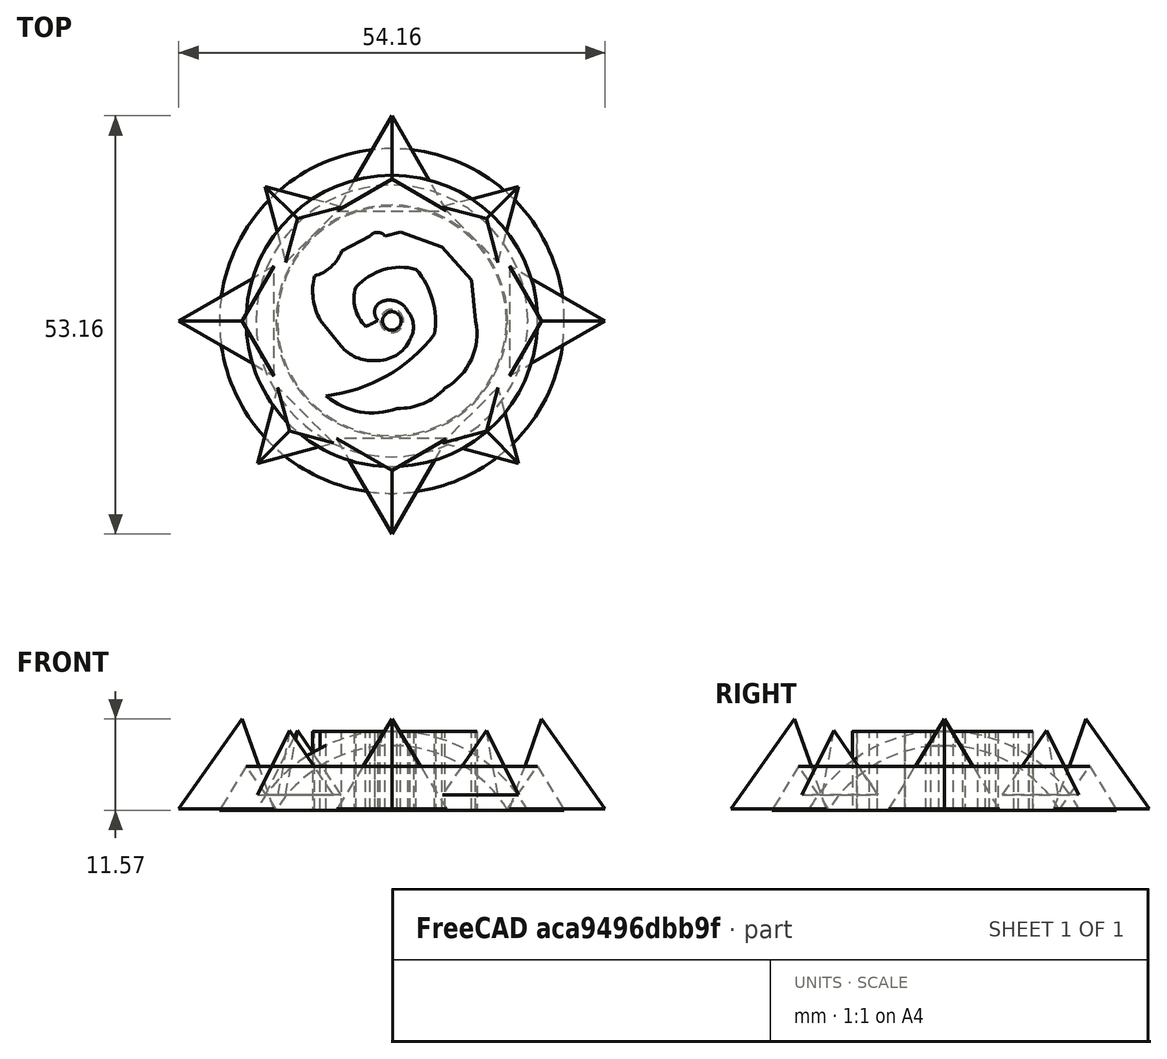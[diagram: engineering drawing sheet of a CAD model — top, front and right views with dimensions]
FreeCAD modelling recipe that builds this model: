
FCSTD DOCUMENT  (FreeCAD 0.19R24291 (Git))
Label: h_brooch_assembly
License: All rights reserved
LicenseURL: http://en.wikipedia.org/wiki/All_rights_reserved
objects: Part::FeaturePython×8, App::DocumentObjectGroup×4, Sketcher::SketchObject×3, PartDesign::Revolution×2, PartDesign::Body×2, Image::ImagePlane×1, Part::Extrusion×1
note: 18 computed .brp shape members not serialized (recipe doc carries the construction recipe); baked Part::Feature solids carry a one-line shape summary decoded from their .brp

FEATURE [Sketcher::SketchObject] Sketch  label="GlowSpiral"
  FullyConstrained = false
  sketch-geometry (22):
    g0: ArcOfCircle CenterX=-0.753903 CenterY=1.11645 CenterZ=0 NormalX=0 NormalY=0 NormalZ=1 AngleXU=0 Radius=1.44543 StartAngle=2.09761 EndAngle=3.93638
    g1: ArcOfCircle CenterX=-0.299965 CenterY=0.00240098 CenterZ=0 NormalX=0 NormalY=0 NormalZ=1 AngleXU=0 Radius=2.64199 StartAngle=0.448711 EndAngle=2.03408
    g2: ArcOfCircle CenterX=-2.56014 CenterY=0.00864041 CenterZ=0 NormalX=0 NormalY=0 NormalZ=1 AngleXU=0 Radius=5.02948 StartAngle=3.82299 EndAngle=4.79664
    g3: ArcOfCircle CenterX=-1.82019 CenterY=-0.475985 CenterZ=0 NormalX=0 NormalY=0 NormalZ=1 AngleXU=0 Radius=4.53808 StartAngle=4.64254 EndAngle=5.86431
    g4: ArcOfCircle CenterX=-0.390387 CenterY=-0.769781 CenterZ=0 NormalX=0 NormalY=0 NormalZ=1 AngleXU=0 Radius=3.12811 StartAngle=5.76403 EndAngle=6.94335
    g5: ArcOfCircle CenterX=1.11392 CenterY=-0.803597 CenterZ=0 NormalX=0 NormalY=0 NormalZ=1 AngleXU=0 Radius=7.62554 StartAngle=1.30785 EndAngle=2.40867
    g6: ArcOfCircle CenterX=-0.0423114 CenterY=2.77393 CenterZ=0 NormalX=0 NormalY=0 NormalZ=1 AngleXU=0 Radius=4.7618 StartAngle=2.81575 EndAngle=3.95354
    g7: ArcOfCircle CenterX=-6.1911 CenterY=7.09486 CenterZ=0 NormalX=0 NormalY=0 NormalZ=1 AngleXU=0 Radius=8.2897 StartAngle=5.06621 EndAngle=5.27544
    g8: ArcOfCircle CenterX=-4.86106 CenterY=-0.147308 CenterZ=0 NormalX=0 NormalY=0 NormalZ=1 AngleXU=0 Radius=10.4068 StartAngle=6.13482 EndAngle=6.98355
    g9: ArcOfCircle CenterX=-10.7491 CenterY=10.7802 CenterZ=0 NormalX=0 NormalY=0 NormalZ=1 AngleXU=0 Radius=20.4256 StartAngle=4.83085 EndAngle=5.62674
    g10: ArcOfCircle CenterX=-2.09735 CenterY=3.86717 CenterZ=0 NormalX=0 NormalY=0 NormalZ=1 AngleXU=0 Radius=7.95781 StartAngle=2.9056 EndAngle=3.63616
    g11: LineSegment StartX=-9.10161 StartY=0.0899867 StartZ=0 EndX=-6.46651 EndY=-3.15932 EndZ=0
    g12: ArcOfCircle CenterX=-11.1957 CenterY=10.7355 CenterZ=0 NormalX=0 NormalY=0 NormalZ=1 AngleXU=0 Radius=5.18935 StartAngle=4.97778 EndAngle=5.91229
    g13: ArcOfCircle CenterX=-1.82628 CenterY=10.0578 CenterZ=0 NormalX=0 NormalY=0 NormalZ=1 AngleXU=0 Radius=1.20224 StartAngle=0.664774 EndAngle=2.5128
    g14: ArcOfCircle CenterX=-2.48457 CenterY=-2.69888 CenterZ=0 NormalX=0 NormalY=0 NormalZ=1 AngleXU=0 Radius=8.97302 StartAngle=4.00215 EndAngle=5.07128
    g15: ArcOfCircle CenterX=0.905868 CenterY=-3.16877 CenterZ=0 NormalX=0 NormalY=0 NormalZ=1 AngleXU=0 Radius=7.93503 StartAngle=4.68229 EndAngle=5.5445
    g16: ArcOfCircle CenterX=2.8748 CenterY=-1.60069 CenterZ=0 NormalX=0 NormalY=0 NormalZ=1 AngleXU=0 Radius=7.93432 StartAngle=5.22593 EndAngle=6.48632
    g17: LineSegment StartX=-6.35919 StartY=8.8546 StartZ=0 EndX=-2.79858 EndY=10.7649 EndZ=0
    g18: LineSegment StartX=1.07314 StartY=11.268 StartZ=0 EndX=6.34907 EndY=9.42071 EndZ=0
    g19: LineSegment StartX=6.34907 StartY=9.42071 StartZ=0 EndX=10.0867 EndY=5.22408 EndZ=0
    g20: LineSegment StartX=10.0867 StartY=5.22408 StartZ=0 EndX=10.646 EndY=0 EndZ=0
    g21: LineSegment StartX=-0.880051 StartY=10.7994 StartZ=0 EndX=1.07314 EndY=11.268 EndZ=0
  constraints (24):
    c: Coincident(g1,g0)
    c: Coincident(g3,g2)
    c: Coincident(g4,g1)
    c: Coincident(g4,g3)
    c: Coincident(g6,g5)
    c: Coincident(g7,g0)
    c: Coincident(g7,g6)
    c: Coincident(g8,g5)
    c: Coincident(g9,g8)
    c: Coincident(g11,g10)
    c: Coincident(g11,g2)
    c: Tangent(g11,g2)
    c: Coincident(g12,g10)
    c: Coincident(g14,g9)
    c: Coincident(g15,g14)
    c: Coincident(g16,g15)
    c: PointOnObject(g16,g-1)
    c: Coincident(g17,g12)
    c: Coincident(g17,g13)
    c: Coincident(g19,g18)
    c: Coincident(g20,g19)
    c: Coincident(g20,g16)
    c: Coincident(g21,g13)
    c: Coincident(g21,g18)
FEATURE [Part::FeaturePython] Tetrahedron  label="Tetra0"  # WARN: FeaturePython — macro-defined, semantics opaque (R4)
  Placement = pos=(0,18,3) rot=(0,0,1;0.523599rad)
  Radius = 8.57321
  Side = 14
FEATURE [Part::FeaturePython] Tetrahedron001  label="Tetra1"  # WARN: FeaturePython — macro-defined, semantics opaque (R4)
  Placement = pos=(0,-19,3) rot=(0,0,-1;0.523599rad)
  Radius = 8.57321
  Side = 14
FEATURE [Sketcher::SketchObject] Sketch001  label="RingCross"
  FullyConstrained = false
  Placement = pos=(0,0,0) rot=(1,0,0;1.5708rad)
  sketch-geometry (3):
    g0: LineSegment StartX=14.5629 StartY=0 StartZ=0 EndX=18.509 EndY=5.58242 EndZ=0
    g1: LineSegment StartX=18.509 StartY=5.58242 StartZ=0 EndX=21.8914 EndY=0 EndZ=0
    g2: LineSegment StartX=21.8914 StartY=0 StartZ=0 EndX=14.5629 EndY=0 EndZ=0
  constraints (5):
    c: PointOnObject(g0,g-1)
    c: Coincident(g1,g0)
    c: PointOnObject(g1,g-1)
    c: Coincident(g2,g1)
    c: Coincident(g2,g0)
FEATURE [PartDesign::Revolution] Revolution
  Angle = 360
  Axis = (0,0,1)
  Base = (0,0,0)
  Placement = pos=(0,0,0) rot=(1,0,0;1.5708rad)
  Profile = -> Sketch001
  ReferenceAxis = -> Sketch001 [V_Axis]
FEATURE [PartDesign::Body] Body  label="OuterRing"
  Group = -> [Sketch001,Revolution]
  Origin = -> Origin
  Tip = -> Revolution
FEATURE [App::DocumentObjectGroup] Group003  label="SweptTri"
  Group = -> [Body]
FEATURE [Part::FeaturePython] Tetrahedron002  label="Tetra2"  # WARN: FeaturePython — macro-defined, semantics opaque (R4)
  Placement = pos=(-19,0,3) rot=(0,0,1;0rad)
  Radius = 8.57321
  Side = 14
FEATURE [Part::FeaturePython] Tetrahedron003  label="Tetra3"  # WARN: FeaturePython — macro-defined, semantics opaque (R4)
  Placement = pos=(19,0,3) rot=(0,0,1;3.14159rad)
  Radius = 8.57321
  Side = 14
FEATURE [App::DocumentObjectGroup] Group  label="OuterTetrahedrals"
  Group = -> [Tetrahedron,Tetrahedron001,Tetrahedron002,Tetrahedron003]
FEATURE [Image::ImagePlane] ImagePlane  label="Hearthstone"
  Placement = pos=(0,-1,0) rot=(0,0,1;0rad)
  XSize = 101.6
  YSize = 57.1
FEATURE [Sketcher::SketchObject] Sketch002  label="dome_slice"
  FullyConstrained = false
  MapMode = 5
  Placement = pos=(0,0,0) rot=(1,0,0;1.5708rad)
  Support = -> [XZ_Plane001]
  sketch-geometry (4):
    g0: ArcOfCircle CenterX=0 CenterY=-9.76772 CenterZ=0 NormalX=0 NormalY=0 NormalZ=1 AngleXU=0 Radius=19.8339 StartAngle=0.514933 EndAngle=1.51134
    g1: ArcOfCircle CenterX=0 CenterY=-9.06492 CenterZ=0 NormalX=0 NormalY=0 NormalZ=1 AngleXU=0 Radius=17.2822 StartAngle=0.552154 EndAngle=1.48438
    g2: LineSegment StartX=1.17848 StartY=10.0311 StartZ=0 EndX=1.49153 EndY=8.15284 EndZ=0
    g3: LineSegment StartX=14.714 StartY=0 StartZ=0 EndX=17.2619 EndY=0 EndZ=0
  constraints (8):
    c: PointOnObject(g0,g-2)
    c: PointOnObject(g0,g-1)
    c: PointOnObject(g1,g-2)
    c: PointOnObject(g1,g-1)
    c: Coincident(g2,g0)
    c: Coincident(g2,g1)
    c: Coincident(g3,g1)
    c: Coincident(g3,g0)
FEATURE [PartDesign::Revolution] Revolution001  label="dome_sweep"
  Angle = 360
  Axis = (0,-2e-16,1)
  Base = (0,0,0)
  Placement = pos=(0,0,0) rot=(1,0,0;1.5708rad)
  Profile = -> Sketch002
  ReferenceAxis = -> Sketch002 [V_Axis]
  Reversed = true
FEATURE [PartDesign::Body] Body001  label="Dome"
  Group = -> [Sketch002,Revolution001]
  Origin = -> Origin001
  Tip = -> Revolution001
FEATURE [Part::FeaturePython] Tetrahedron004  label="Tetra004"  # WARN: FeaturePython — macro-defined, semantics opaque (R4)
  Placement = pos=(12,13,4) rot=(0,0,-1;0.261799rad)
  Radius = 6.12372
  Side = 10
FEATURE [Part::FeaturePython] Tetrahedron005  label="Tetra005"  # WARN: FeaturePython — macro-defined, semantics opaque (R4)
  Placement = pos=(-12,13,4) rot=(0,0,-1;0.785398rad)
  Radius = 6.12372
  Side = 10
FEATURE [Part::FeaturePython] Tetrahedron006  label="Tetra006"  # WARN: FeaturePython — macro-defined, semantics opaque (R4)
  Placement = pos=(12,-14,4) rot=(0,0,1;0.261799rad)
  Radius = 6.12372
  Side = 10
FEATURE [Part::FeaturePython] Tetrahedron007  label="Tetra007"  # WARN: FeaturePython — macro-defined, semantics opaque (R4)
  Placement = pos=(-13,-14,4) rot=(0,0,-1;1.309rad)
  Radius = 6.12372
  Side = 10
FEATURE [App::DocumentObjectGroup] Group002  label="InnerTetrahedrals"
  Group = -> [Tetrahedron004,Tetrahedron005,Tetrahedron006,Tetrahedron007]
FEATURE [Part::Extrusion] Extrude  label="GlowExtrude"
  Base = -> Sketch
  Dir = (0,0,1)
  DirMode = 0
  FaceMakerClass = Part::FaceMakerBullseye
  LengthFwd = 10
  LengthRev = 0
  Solid = true
  Symmetric = false
FEATURE [App::DocumentObjectGroup] Group001  label="Cabuchon"
  Group = -> [Body001,Sketch,Extrude]
